annotation { "Feature Type Name" : "Feature", "Feature Type Description" : "" }
export const myFeature = defineFeature(function(context is Context, id is Id, definition is map)
    precondition{}
    {
        {
            var Q0;
            Q0=qCreatedBy(makeId("Front.planeOp"),FACE);
            var sketch = newSketch(context, id + "F0", { "sketchPlane" : qUnion([Q0])});
            skLineSegment(sketch, "E0.bottom", {"start": v(0, 0) * mm, "end": v(7620, 0) * mm, "construction": true});
            skLineSegment(sketch, "E0.top", {"start": v(0, -5080) * mm, "end": v(7620, -5080) * mm, "construction": true});
            skLineSegment(sketch, "E0.left", {"start": v(0, 0) * mm, "end": v(0, -5080) * mm, "construction": true});
            skLineSegment(sketch, "E0.right", {"start": v(7620, 0) * mm, "end": v(7620, -5080) * mm, "construction": true});
            skLineSegment(sketch, "E1", {"start": v(549.43, -5080) * mm, "end": v(549.43, -1016) * mm});
            skLineSegment(sketch, "E2", {"start": v(549.43, -1016) * mm, "end": v(208.88, -1016) * mm});
            skLineSegment(sketch, "E3", {"start": v(208.88, -1016) * mm, "end": v(549.43, -508) * mm});
            skLineSegment(sketch, "E4", {"start": v(549.43, -508) * mm, "end": v(2835.43, -508) * mm});
            skLineSegment(sketch, "E5", {"start": v(2835.43, -508) * mm, "end": v(2835.43, -399.02) * mm});
            skLineSegment(sketch, "E6", {"start": v(2835.43, -399.02) * mm, "end": v(4107.36, -399.02) * mm});
            skLineSegment(sketch, "E7", {"start": v(4107.36, -399.02) * mm, "end": v(4107.36, -508) * mm});
            skLineSegment(sketch, "E8", {"start": v(4107.36, -508) * mm, "end": v(6393.36, -508) * mm});
            skLineSegment(sketch, "E9", {"start": v(6393.36, -508) * mm, "end": v(6624.94, -807.69) * mm});
            skLineSegment(sketch, "E10", {"start": v(549.43, -1016) * mm, "end": v(6393.36, -1016) * mm});
            skPoint(sketch, "E11.start.orphan", {"position": v(6393.36, -879.78) * mm});
            skPoint(sketch, "E12.start.orphan", {"position": v(6771.67, -1016) * mm});
            skLineSegment(sketch, "E13", {"start": v(6393.36, -1016) * mm, "end": v(6457.69, -5080) * mm});
            skPoint(sketch, "E14.end.orphan", {"position": v(6771.67, -1077.69) * mm});
            skLineSegment(sketch, "E15", {"start": v(6393.36, -1016) * mm, "end": v(6695.3, -1016) * mm});
            skLineSegment(sketch, "E16", {"start": v(6624.94, -807.69) * mm, "end": v(6695.3, -1016) * mm});
            skLineSegment(sketch, "E17", {"start": v(549.43, -5080) * mm, "end": v(6457.69, -5080) * mm});
            skText(sketch, "E18", { "text": "Caesars Palace", "fontName": "OpenSans-Regular.ttf"});
            skLineSegment(sketch, "E19", {"start": v(869.45, -1935.26) * mm, "end": v(869.45, -2701.87) * mm});
            const initialGuessF0  = {"E18": [0.60938, -1.70855, 1, 0, 0.59401]};
            skSetInitialGuess(sketch, initialGuessF0);
            skSolve(sketch);
        }
        {
            var Q0;
            Q0=makeQuery(id+"F0.imprint","IMPRINT",FACE,{"disambiguationData":[TD([[makeQuery(id+"F0.imprint","IMPRINT",EDGE,{"derivedFrom":sQuery(id+"F0.wireOp",EDGE,"E2")}),-1.0]])]});
            var Q1;
            Q1=makeQuery(id+"F0.imprint","IMPRINT",FACE,{"disambiguationData":[TD([[makeQuery(id+"F0.imprint","IMPRINT",EDGE,{"derivedFrom":sQuery(id+"F0.wireOp",EDGE,"E1")}),-1.0]])]});
            var Q2;
            Q2=makeQuery(id+"F0.imprint","IMPRINT",FACE,{"disambiguationData":[TD([[makeQuery(id+"F0.imprint","IMPRINT",EDGE,{"derivedFrom":sQuery(id+"F0.wireOp",EDGE,"KvOMIhKF-PHGV-okiL-ZL8v-noESfuEzF9ne")}),1.0]])]});
            var Q3;
            {var subQ0=sQuery(id+"F0.wireOp",EDGE,"hjMhRz81-y2WC-o3FO-r4DJ-aUPkSPwPc6w1");var subQ1=sQuery(id+"F0.wireOp",EDGE,"PUnVNprd-wIhr-td4K-ZOek-EyB3BgGaWvDh");var subQ2=makeQuery(id+"F0.imprint","INTERSECT",VERTEX,{"derivedFrom":[subQ1,subQ0]});Q3=makeQuery(id+"F0.imprint","IMPRINT",FACE,{"disambiguationData":[TD([[makeQuery(id+"F0.imprint","IMPRINT",EDGE,{"disambiguationData":[TD([[subQ2,1.0]])],"derivedFrom":subQ1}),-1.0]])]});}
            var Q4;
            {var subQ3=sQuery(id+"F0.wireOp",EDGE,"14k7XJXQ-udJs-1N83-N1wx-IxI8iWN5m4M2");Q4=makeQuery(id+"F0.imprint","IMPRINT",FACE,{"disambiguationData":[TD([[makeQuery(id+"F0.imprint","IMPRINT",EDGE,{"derivedFrom":subQ3}),1.0]])]});}
            var Q5;
            {var subQ0=sQuery(id+"F0.wireOp",EDGE,"AsiQ61zh-l65h-7OTK-XggF-ZhWAl5ibSfz3");Q5=makeQuery(id+"F0.imprint","IMPRINT",FACE,{"disambiguationData":[TD([[makeQuery(id+"F0.imprint","IMPRINT",EDGE,{"derivedFrom":subQ0}),1.0]])]});}
            var Q6;
            {var subQ3=sQuery(id+"F0.wireOp",EDGE,"ECTPYI1q-8gZe-Z5w7-Ljkz-XwgWXzBHBB5x");Q6=makeQuery(id+"F0.imprint","IMPRINT",FACE,{"disambiguationData":[TD([[makeQuery(id+"F0.imprint","IMPRINT",EDGE,{"derivedFrom":subQ3}),1.0]])]});}
            var Q7;
            {var subQ0=sQuery(id+"F0.wireOp",EDGE,"HDrfkN6y-VysE-4T87-BnAI-6j7e9yGuQCwg");var subQ1=sQuery(id+"F0.wireOp",EDGE,"2nFrvyrv-Lrbe-R9Ou-C0bK-kZpyZilrZiLl");var subQ2=makeQuery(id+"F0.imprint","INTERSECT",VERTEX,{"derivedFrom":[subQ1,subQ0]});Q7=makeQuery(id+"F0.imprint","IMPRINT",FACE,{"disambiguationData":[TD([[makeQuery(id+"F0.imprint","IMPRINT",EDGE,{"disambiguationData":[TD([[subQ2,-1.0]])],"derivedFrom":subQ1}),1.0]])]});}
            var Q8;
            Q8=makeQuery(id+"F0.imprint","IMPRINT",FACE,{"disambiguationData":[TD([[makeQuery(id+"F0.imprint","IMPRINT",EDGE,{"derivedFrom":sQuery(id+"F0.wireOp",EDGE,"wiCc5QsL-rsDi-XcWj-8SFZ-K9Qo260RabNm")}),1.0]])]});
            var Q9;
            Q9=makeQuery(id+"F0.imprint","IMPRINT",FACE,{"disambiguationData":[TD([[makeQuery(id+"F0.imprint","IMPRINT",EDGE,{"derivedFrom":sQuery(id+"F0.wireOp",EDGE,"WployQqh-umqh-zA3T-6Un7-jpEjEAPBqfzf")}),1.0]])]});
            extrude(context, id + "F1", {"entities" : qUnion([Q0, Q1, Q2, Q3, Q4, Q5, Q6, Q7, Q8, Q9]), "depth" : 1879.6 * mm, "offsetDistance" : 25.4 * mm});
        }
        {
            var Q0;
            Q0=makeQuery(id+"F1.opExtrude","CAP_FACE",FACE,{"disambiguationData":[OSD([sQuery(id+"F0.wireOp",EDGE,"E1"),sQuery(id+"F0.wireOp",EDGE,"E2"),sQuery(id+"F0.wireOp",EDGE,"E3"),sQuery(id+"F0.wireOp",EDGE,"E4"),sQuery(id+"F0.wireOp",EDGE,"E5"),sQuery(id+"F0.wireOp",EDGE,"E6"),sQuery(id+"F0.wireOp",EDGE,"E7"),sQuery(id+"F0.wireOp",EDGE,"E8"),sQuery(id+"F0.wireOp",EDGE,"E9"),sQuery(id+"F0.wireOp",EDGE,"E13"),sQuery(id+"F0.wireOp",EDGE,"E15"),sQuery(id+"F0.wireOp",EDGE,"E16"),sQuery(id+"F0.wireOp",EDGE,"E17"),sQuery(id+"F0.wireOp",EDGE,"E18.sketch_text.stroke-0"),sQuery(id+"F0.wireOp",EDGE,"E18.sketch_text.stroke-1"),sQuery(id+"F0.wireOp",EDGE,"E18.sketch_text.stroke-2"),sQuery(id+"F0.wireOp",EDGE,"E18.sketch_text.stroke-3"),sQuery(id+"F0.wireOp",EDGE,"E18.sketch_text.stroke-4"),sQuery(id+"F0.wireOp",EDGE,"E18.sketch_text.stroke-5"),sQuery(id+"F0.wireOp",EDGE,"E18.sketch_text.stroke-6"),sQuery(id+"F0.wireOp",EDGE,"E18.sketch_text.stroke-7"),sQuery(id+"F0.wireOp",EDGE,"E18.sketch_text.stroke-8"),sQuery(id+"F0.wireOp",EDGE,"E18.sketch_text.stroke-9"),sQuery(id+"F0.wireOp",EDGE,"E18.sketch_text.stroke-10"),sQuery(id+"F0.wireOp",EDGE,"E18.sketch_text.stroke-11"),sQuery(id+"F0.wireOp",EDGE,"E18.sketch_text.stroke-12"),sQuery(id+"F0.wireOp",EDGE,"E18.sketch_text.stroke-13"),sQuery(id+"F0.wireOp",EDGE,"E18.sketch_text.stroke-14"),sQuery(id+"F0.wireOp",EDGE,"E18.sketch_text.stroke-15"),sQuery(id+"F0.wireOp",EDGE,"E18.sketch_text.stroke-16"),sQuery(id+"F0.wireOp",EDGE,"E18.sketch_text.stroke-17"),sQuery(id+"F0.wireOp",EDGE,"E18.sketch_text.stroke-18"),sQuery(id+"F0.wireOp",EDGE,"E18.sketch_text.stroke-19"),sQuery(id+"F0.wireOp",EDGE,"E18.sketch_text.stroke-20"),sQuery(id+"F0.wireOp",EDGE,"E18.sketch_text.stroke-21"),sQuery(id+"F0.wireOp",EDGE,"E18.sketch_text.stroke-22"),sQuery(id+"F0.wireOp",EDGE,"E18.sketch_text.stroke-23"),sQuery(id+"F0.wireOp",EDGE,"E18.sketch_text.stroke-24"),sQuery(id+"F0.wireOp",EDGE,"E18.sketch_text.stroke-25"),sQuery(id+"F0.wireOp",EDGE,"E18.sketch_text.stroke-26"),sQuery(id+"F0.wireOp",EDGE,"E18.sketch_text.stroke-27"),sQuery(id+"F0.wireOp",EDGE,"E18.sketch_text.stroke-28"),sQuery(id+"F0.wireOp",EDGE,"E18.sketch_text.stroke-29"),sQuery(id+"F0.wireOp",EDGE,"E18.sketch_text.stroke-30"),sQuery(id+"F0.wireOp",EDGE,"E18.sketch_text.stroke-31"),sQuery(id+"F0.wireOp",EDGE,"E18.sketch_text.stroke-32"),sQuery(id+"F0.wireOp",EDGE,"E18.sketch_text.stroke-33"),sQuery(id+"F0.wireOp",EDGE,"E18.sketch_text.stroke-42"),sQuery(id+"F0.wireOp",EDGE,"E18.sketch_text.stroke-43"),sQuery(id+"F0.wireOp",EDGE,"E18.sketch_text.stroke-44"),sQuery(id+"F0.wireOp",EDGE,"E18.sketch_text.stroke-45"),sQuery(id+"F0.wireOp",EDGE,"E18.sketch_text.stroke-46"),sQuery(id+"F0.wireOp",EDGE,"E18.sketch_text.stroke-47"),sQuery(id+"F0.wireOp",EDGE,"E18.sketch_text.stroke-48"),sQuery(id+"F0.wireOp",EDGE,"E18.sketch_text.stroke-49"),sQuery(id+"F0.wireOp",EDGE,"E18.sketch_text.stroke-50"),sQuery(id+"F0.wireOp",EDGE,"E18.sketch_text.stroke-51"),sQuery(id+"F0.wireOp",EDGE,"E18.sketch_text.stroke-52"),sQuery(id+"F0.wireOp",EDGE,"E18.sketch_text.stroke-53"),sQuery(id+"F0.wireOp",EDGE,"E18.sketch_text.stroke-54"),sQuery(id+"F0.wireOp",EDGE,"E18.sketch_text.stroke-55"),sQuery(id+"F0.wireOp",EDGE,"E18.sketch_text.stroke-61"),sQuery(id+"F0.wireOp",EDGE,"E18.sketch_text.stroke-62"),sQuery(id+"F0.wireOp",EDGE,"E18.sketch_text.stroke-63"),sQuery(id+"F0.wireOp",EDGE,"E18.sketch_text.stroke-64"),sQuery(id+"F0.wireOp",EDGE,"E18.sketch_text.stroke-65"),sQuery(id+"F0.wireOp",EDGE,"E18.sketch_text.stroke-66"),sQuery(id+"F0.wireOp",EDGE,"E18.sketch_text.stroke-67"),sQuery(id+"F0.wireOp",EDGE,"E18.sketch_text.stroke-68"),sQuery(id+"F0.wireOp",EDGE,"E18.sketch_text.stroke-69"),sQuery(id+"F0.wireOp",EDGE,"E18.sketch_text.stroke-70"),sQuery(id+"F0.wireOp",EDGE,"E18.sketch_text.stroke-71"),sQuery(id+"F0.wireOp",EDGE,"E18.sketch_text.stroke-72"),sQuery(id+"F0.wireOp",EDGE,"E18.sketch_text.stroke-73"),sQuery(id+"F0.wireOp",EDGE,"E18.sketch_text.stroke-74"),sQuery(id+"F0.wireOp",EDGE,"E18.sketch_text.stroke-75"),sQuery(id+"F0.wireOp",EDGE,"E18.sketch_text.stroke-76"),sQuery(id+"F0.wireOp",EDGE,"E18.sketch_text.stroke-77"),sQuery(id+"F0.wireOp",EDGE,"E18.sketch_text.stroke-78"),sQuery(id+"F0.wireOp",EDGE,"E18.sketch_text.stroke-79"),sQuery(id+"F0.wireOp",EDGE,"E18.sketch_text.stroke-80"),sQuery(id+"F0.wireOp",EDGE,"E18.sketch_text.stroke-81"),sQuery(id+"F0.wireOp",EDGE,"E18.sketch_text.stroke-82"),sQuery(id+"F0.wireOp",EDGE,"E18.sketch_text.stroke-83"),sQuery(id+"F0.wireOp",EDGE,"E18.sketch_text.stroke-84"),sQuery(id+"F0.wireOp",EDGE,"E18.sketch_text.stroke-85"),sQuery(id+"F0.wireOp",EDGE,"E18.sketch_text.stroke-86"),sQuery(id+"F0.wireOp",EDGE,"E18.sketch_text.stroke-87"),sQuery(id+"F0.wireOp",EDGE,"E18.sketch_text.stroke-88"),sQuery(id+"F0.wireOp",EDGE,"E18.sketch_text.stroke-89"),sQuery(id+"F0.wireOp",EDGE,"E18.sketch_text.stroke-90"),sQuery(id+"F0.wireOp",EDGE,"E18.sketch_text.stroke-91"),sQuery(id+"F0.wireOp",EDGE,"E18.sketch_text.stroke-92"),sQuery(id+"F0.wireOp",EDGE,"E18.sketch_text.stroke-93"),sQuery(id+"F0.wireOp",EDGE,"E18.sketch_text.stroke-94"),sQuery(id+"F0.wireOp",EDGE,"E18.sketch_text.stroke-95"),sQuery(id+"F0.wireOp",EDGE,"E18.sketch_text.stroke-96"),sQuery(id+"F0.wireOp",EDGE,"E18.sketch_text.stroke-97"),sQuery(id+"F0.wireOp",EDGE,"E18.sketch_text.stroke-98"),sQuery(id+"F0.wireOp",EDGE,"E18.sketch_text.stroke-99"),sQuery(id+"F0.wireOp",EDGE,"E18.sketch_text.stroke-100"),sQuery(id+"F0.wireOp",EDGE,"E18.sketch_text.stroke-101"),sQuery(id+"F0.wireOp",EDGE,"E18.sketch_text.stroke-102"),sQuery(id+"F0.wireOp",EDGE,"E18.sketch_text.stroke-103"),sQuery(id+"F0.wireOp",EDGE,"E18.sketch_text.stroke-104"),sQuery(id+"F0.wireOp",EDGE,"E18.sketch_text.stroke-113"),sQuery(id+"F0.wireOp",EDGE,"E18.sketch_text.stroke-114"),sQuery(id+"F0.wireOp",EDGE,"E18.sketch_text.stroke-115"),sQuery(id+"F0.wireOp",EDGE,"E18.sketch_text.stroke-116"),sQuery(id+"F0.wireOp",EDGE,"E18.sketch_text.stroke-117"),sQuery(id+"F0.wireOp",EDGE,"E18.sketch_text.stroke-118"),sQuery(id+"F0.wireOp",EDGE,"E18.sketch_text.stroke-119"),sQuery(id+"F0.wireOp",EDGE,"E18.sketch_text.stroke-120"),sQuery(id+"F0.wireOp",EDGE,"E18.sketch_text.stroke-121"),sQuery(id+"F0.wireOp",EDGE,"E18.sketch_text.stroke-122"),sQuery(id+"F0.wireOp",EDGE,"E18.sketch_text.stroke-123"),sQuery(id+"F0.wireOp",EDGE,"E18.sketch_text.stroke-124"),sQuery(id+"F0.wireOp",EDGE,"E18.sketch_text.stroke-125"),sQuery(id+"F0.wireOp",EDGE,"E18.sketch_text.stroke-126"),sQuery(id+"F0.wireOp",EDGE,"E18.sketch_text.stroke-127"),sQuery(id+"F0.wireOp",EDGE,"E18.sketch_text.stroke-128"),sQuery(id+"F0.wireOp",EDGE,"E18.sketch_text.stroke-129"),sQuery(id+"F0.wireOp",EDGE,"E18.sketch_text.stroke-130"),sQuery(id+"F0.wireOp",EDGE,"E18.sketch_text.stroke-131"),sQuery(id+"F0.wireOp",EDGE,"E18.sketch_text.stroke-132"),sQuery(id+"F0.wireOp",EDGE,"E18.sketch_text.stroke-133"),sQuery(id+"F0.wireOp",EDGE,"E18.sketch_text.stroke-134"),sQuery(id+"F0.wireOp",EDGE,"E18.sketch_text.stroke-135"),sQuery(id+"F0.wireOp",EDGE,"E18.sketch_text.stroke-136"),sQuery(id+"F0.wireOp",EDGE,"E18.sketch_text.stroke-137"),sQuery(id+"F0.wireOp",EDGE,"E18.sketch_text.stroke-138"),sQuery(id+"F0.wireOp",EDGE,"E18.sketch_text.stroke-139"),sQuery(id+"F0.wireOp",EDGE,"E18.sketch_text.stroke-140"),sQuery(id+"F0.wireOp",EDGE,"E18.sketch_text.stroke-141"),sQuery(id+"F0.wireOp",EDGE,"E18.sketch_text.stroke-142"),sQuery(id+"F0.wireOp",EDGE,"E18.sketch_text.stroke-143"),sQuery(id+"F0.wireOp",EDGE,"E18.sketch_text.stroke-144"),sQuery(id+"F0.wireOp",EDGE,"E18.sketch_text.stroke-145"),sQuery(id+"F0.wireOp",EDGE,"E18.sketch_text.stroke-146"),sQuery(id+"F0.wireOp",EDGE,"E18.sketch_text.stroke-147"),sQuery(id+"F0.wireOp",EDGE,"E18.sketch_text.stroke-148"),sQuery(id+"F0.wireOp",EDGE,"E18.sketch_text.stroke-149"),sQuery(id+"F0.wireOp",EDGE,"E18.sketch_text.stroke-150"),sQuery(id+"F0.wireOp",EDGE,"E18.sketch_text.stroke-151"),sQuery(id+"F0.wireOp",EDGE,"E18.sketch_text.stroke-152"),sQuery(id+"F0.wireOp",EDGE,"E18.sketch_text.stroke-153"),sQuery(id+"F0.wireOp",EDGE,"E18.sketch_text.stroke-154"),sQuery(id+"F0.wireOp",EDGE,"E18.sketch_text.stroke-155"),sQuery(id+"F0.wireOp",EDGE,"E18.sketch_text.stroke-156"),sQuery(id+"F0.wireOp",EDGE,"E18.sketch_text.stroke-157"),sQuery(id+"F0.wireOp",EDGE,"E18.sketch_text.stroke-158"),sQuery(id+"F0.wireOp",EDGE,"E18.sketch_text.stroke-166"),sQuery(id+"F0.wireOp",EDGE,"E18.sketch_text.stroke-167"),sQuery(id+"F0.wireOp",EDGE,"E18.sketch_text.stroke-168"),sQuery(id+"F0.wireOp",EDGE,"E18.sketch_text.stroke-169"),sQuery(id+"F0.wireOp",EDGE,"E18.sketch_text.stroke-170"),sQuery(id+"F0.wireOp",EDGE,"E18.sketch_text.stroke-171"),sQuery(id+"F0.wireOp",EDGE,"E18.sketch_text.stroke-172"),sQuery(id+"F0.wireOp",EDGE,"E18.sketch_text.stroke-173"),sQuery(id+"F0.wireOp",EDGE,"E18.sketch_text.stroke-174"),sQuery(id+"F0.wireOp",EDGE,"E18.sketch_text.stroke-175"),sQuery(id+"F0.wireOp",EDGE,"E18.sketch_text.stroke-176"),sQuery(id+"F0.wireOp",EDGE,"E18.sketch_text.stroke-177"),sQuery(id+"F0.wireOp",EDGE,"E18.sketch_text.stroke-178"),sQuery(id+"F0.wireOp",EDGE,"E18.sketch_text.stroke-179"),sQuery(id+"F0.wireOp",EDGE,"E18.sketch_text.stroke-180"),sQuery(id+"F0.wireOp",EDGE,"E18.sketch_text.stroke-181"),sQuery(id+"F0.wireOp",EDGE,"E18.sketch_text.stroke-182"),sQuery(id+"F0.wireOp",EDGE,"E18.sketch_text.stroke-183"),sQuery(id+"F0.wireOp",EDGE,"E18.sketch_text.stroke-184"),sQuery(id+"F0.wireOp",EDGE,"E18.sketch_text.stroke-193"),sQuery(id+"F0.wireOp",EDGE,"E18.sketch_text.stroke-194"),sQuery(id+"F0.wireOp",EDGE,"E18.sketch_text.stroke-195"),sQuery(id+"F0.wireOp",EDGE,"E18.sketch_text.stroke-196"),sQuery(id+"F0.wireOp",EDGE,"E18.sketch_text.stroke-197"),sQuery(id+"F0.wireOp",EDGE,"E18.sketch_text.stroke-198"),sQuery(id+"F0.wireOp",EDGE,"E18.sketch_text.stroke-199"),sQuery(id+"F0.wireOp",EDGE,"E18.sketch_text.stroke-200"),sQuery(id+"F0.wireOp",EDGE,"E18.sketch_text.stroke-201"),sQuery(id+"F0.wireOp",EDGE,"E18.sketch_text.stroke-202"),sQuery(id+"F0.wireOp",EDGE,"E18.sketch_text.stroke-203"),sQuery(id+"F0.wireOp",EDGE,"E18.sketch_text.stroke-204"),sQuery(id+"F0.wireOp",EDGE,"E18.sketch_text.stroke-205"),sQuery(id+"F0.wireOp",EDGE,"E18.sketch_text.stroke-206"),sQuery(id+"F0.wireOp",EDGE,"E18.sketch_text.stroke-207"),sQuery(id+"F0.wireOp",EDGE,"E18.sketch_text.stroke-208"),sQuery(id+"F0.wireOp",EDGE,"E18.sketch_text.stroke-209"),sQuery(id+"F0.wireOp",EDGE,"E18.sketch_text.stroke-210"),sQuery(id+"F0.wireOp",EDGE,"E18.sketch_text.stroke-211"),sQuery(id+"F0.wireOp",EDGE,"E18.sketch_text.stroke-212"),sQuery(id+"F0.wireOp",EDGE,"E18.sketch_text.stroke-213"),sQuery(id+"F0.wireOp",EDGE,"E18.sketch_text.stroke-214"),sQuery(id+"F0.wireOp",EDGE,"E18.sketch_text.stroke-215"),sQuery(id+"F0.wireOp",EDGE,"E18.sketch_text.stroke-224"),sQuery(id+"F0.wireOp",EDGE,"E18.sketch_text.stroke-225"),sQuery(id+"F0.wireOp",EDGE,"E18.sketch_text.stroke-226"),sQuery(id+"F0.wireOp",EDGE,"E18.sketch_text.stroke-227"),sQuery(id+"F0.wireOp",EDGE,"E18.sketch_text.stroke-228"),sQuery(id+"F0.wireOp",EDGE,"E18.sketch_text.stroke-229"),sQuery(id+"F0.wireOp",EDGE,"E18.sketch_text.stroke-230"),sQuery(id+"F0.wireOp",EDGE,"E18.sketch_text.stroke-231"),sQuery(id+"F0.wireOp",EDGE,"E18.sketch_text.stroke-232"),sQuery(id+"F0.wireOp",EDGE,"E18.sketch_text.stroke-233"),sQuery(id+"F0.wireOp",EDGE,"E18.sketch_text.stroke-234"),sQuery(id+"F0.wireOp",EDGE,"E18.sketch_text.stroke-235"),sQuery(id+"F0.wireOp",EDGE,"E18.sketch_text.stroke-236"),sQuery(id+"F0.wireOp",EDGE,"E18.sketch_text.stroke-237"),sQuery(id+"F0.wireOp",EDGE,"E18.sketch_text.stroke-238"),sQuery(id+"F0.wireOp",EDGE,"E18.sketch_text.stroke-239"),sQuery(id+"F0.wireOp",EDGE,"E18.sketch_text.stroke-240"),sQuery(id+"F0.wireOp",EDGE,"E18.sketch_text.stroke-241"),sQuery(id+"F0.wireOp",EDGE,"E18.sketch_text.stroke-242"),sQuery(id+"F0.wireOp",EDGE,"E18.sketch_text.stroke-243"),sQuery(id+"F0.wireOp",EDGE,"E18.sketch_text.stroke-244"),sQuery(id+"F0.wireOp",EDGE,"E18.sketch_text.stroke-245"),sQuery(id+"F0.wireOp",EDGE,"E18.sketch_text.stroke-246"),sQuery(id+"F0.wireOp",EDGE,"E18.sketch_text.stroke-247"),sQuery(id+"F0.wireOp",EDGE,"E18.sketch_text.stroke-248"),sQuery(id+"F0.wireOp",EDGE,"E18.sketch_text.stroke-249"),sQuery(id+"F0.wireOp",EDGE,"E18.sketch_text.stroke-250"),sQuery(id+"F0.wireOp",EDGE,"E18.sketch_text.stroke-251"),sQuery(id+"F0.wireOp",EDGE,"E18.sketch_text.stroke-252")])],"isStart":false});
            var sketch = newSketch(context, id + "F2", { "sketchPlane" : qUnion([Q0])});
            skCircle(sketch, "E20", {"center": v(4356.6, -4060.87) * mm, "radius": 54.94 * mm});
            skCircle(sketch, "E21", {"center": v(4086.02, -3810.31) * mm, "radius": 50.8 * mm});
            skCircle(sketch, "E22", {"center": v(4086.02, -3556.31) * mm, "radius": 50.8 * mm});
            skCircle(sketch, "E23", {"center": v(4102.62, -4064.31) * mm, "radius": 50.8 * mm});
            skCircle(sketch, "E24", {"center": v(4102.62, -4318.31) * mm, "radius": 50.8 * mm});
            skSolve(sketch);
        }
        {
            var Q0;
            Q0 = qSketchRegion(id + "F2", true);
            extrude(context, id + "F3", {"entities" : qUnion([Q0]), "operationType" : NewBodyOperationType.REMOVE, "oppositeDirection" : true, "depth" : 4038.6 * mm, "offsetDistance" : 25.4 * mm});
        }
        {
            var Q0;
            Q0=makeQuery(id+"F2.imprint","IMPRINT",FACE,{"disambiguationData":[TD([[makeQuery(id+"F2.imprint","IMPRINT",EDGE,{"derivedFrom":sQuery(id+"F2.wireOp",EDGE,"E20")}),-1.0]])]});
            var sketch = newSketch(context, id + "F4", { "sketchPlane" : qUnion([Q0])});
            skLineSegment(sketch, "E25", {"start": v(5061.76, -3432.2) * mm, "end": v(5061.76, -3914.8) * mm});
            skLineSegment(sketch, "E26", {"start": v(5061.76, -3432.2) * mm, "end": v(6357.16, -3432.2) * mm});
            skLineSegment(sketch, "E27", {"start": v(6357.16, -3432.2) * mm, "end": v(6357.16, -3914.8) * mm});
            skLineSegment(sketch, "E28", {"start": v(5061.76, -3914.8) * mm, "end": v(6357.16, -3914.8) * mm});
            skSolve(sketch);
        }
        {
            var Q0;
            Q0 = qSketchRegion(id + "F4", true);
            extrude(context, id + "F5", {"entities" : qUnion([Q0]), "operationType" : NewBodyOperationType.REMOVE, "oppositeDirection" : true, "depth" : 2717.8 * mm, "offsetDistance" : 25.4 * mm});
        }
        {
            var Q0;
            Q0=makeQuery(id+"F2.imprint","IMPRINT",FACE,{"disambiguationData":[TD([[makeQuery(id+"F2.imprint","IMPRINT",EDGE,{"derivedFrom":sQuery(id+"F2.wireOp",EDGE,"E20")}),-1.0]])]});
            var sketch = newSketch(context, id + "F6", { "sketchPlane" : qUnion([Q0])});
            skCircle(sketch, "E29", {"center": v(4476.23, -4440.93) * mm, "radius": 152.4 * mm});
            skSolve(sketch);
        }
        {
            var Q0;
            Q0 = qSketchRegion(id + "F6", true);
            extrude(context, id + "F7", {"entities" : qUnion([Q0]), "operationType" : NewBodyOperationType.REMOVE, "oppositeDirection" : true, "depth" : 3378.2 * mm, "offsetDistance" : 25.4 * mm});
        }
    });